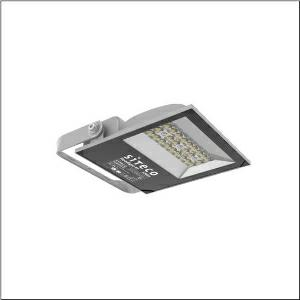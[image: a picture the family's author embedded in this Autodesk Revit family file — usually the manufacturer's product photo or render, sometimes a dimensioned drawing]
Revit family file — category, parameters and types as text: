
# Revit family: floodlight_fl_41_mini___pl32_5xa8571a2121_f875
name_source: partatom
category: Lighting Fixtures
units: mm (PartAtom-declared; Revit-internal decimal feet)

## family parameters
Cut with Voids When Loaded = No
Host = Face
Light Source = No
Part Type = Normal
Room Calculation Point = No
Round Connector Dimension = Use Diameter
Shared = No

## types (1)
- --- (1 x LED, 13000 lm, 100 W, 4000K)
    Apparent Load = 100 VA
    CIE Flux Codes = 40 79 99 100 100
    Color Rendering = 70
    Color Temperature = 4000K
    Default Elevation = 1800 mm
    Description = Floodlight FL 41 mini, floodlight, primary light control with lens, of PMMA, primary optical cover: protective disc, transparent, light distribution: PL32, light emission: direct distribution, installation type: surface-mounted, LED, High Power LED, rated luminous flux: 13.000lm, luminous efficacy: 130lm/W, light colour: 740, colour temperature: 4000K, control gear: ON/OFF Multilumen, with cable, 3x 1.5mm², mains connection: 220..240V, AC, 50/60Hz, connection cable pre-assembled, cable length: 2m, rated input power: 100W, luminaire housing, of diecast aluminium, powder-coated, metallic grey (RAL 9006), length: 265mm, width: 245mm, height: 54mm, protection rating (complete): IP65, insulation class (complete): insulation class I (protective earthing), certification: CE, ENEC, impact resistance: IK08, permissible operating ambient temperature: -40..+40°C, permissible storage temperature: -40..+60°C, packaging unit: 1 piece

Light Distribution: PL32
    Height = 54 mm
    Lamp = 1 x LED
    Lamp Light Flux = 13000 lm
    Lamp Power = 100 W
    Lamp count = 1
    Length = 226 mm
    Luminous efficacy = 130 lm/W
    Manufacturer = Siteco
    ModVariant = No
    Model = 5XA8571A2121
    Mounting Place = Ceiling
    Mounting Type = Surface mounted
    Number of Poles = 1
    OnlyDefault = Yes
    Power Factor = 1
    Product Name = Floodlight FL 41 mini | PL32
    Product group = floodlight | ceiling mounted
    ProductGroupID = 302
    Protection Class = Protection class I
    Protection Degree = IP 65
    RLX_Detail_Level = 1
    RLX_Emergency_Light_Flux = 0 lm
    RLX_Emergency_Type = 0
    RLX_Emergency_Type_DB = No
    RlxData = <blob elided: 24633 chars, md5=8b342c8b>
    Socket = socket
    Standby Power = 0 W
    System Light Flux = 13000 lm
    System Power = 100 W
    Type Comments = factory setting: luminous flux: 100 % | (OFF | OFF | OFF)
    Type Image = l_1248226.jpg
    URL = http://relux.com
    VarID = @adj_153151
    Voltage = 0 V
    Weight = 0.00 kg
    Width = 241 mm

## geometry (parser evidence)
native form markers: Blend x4, Sweep x13
no freeform markers — native parametric forms only
